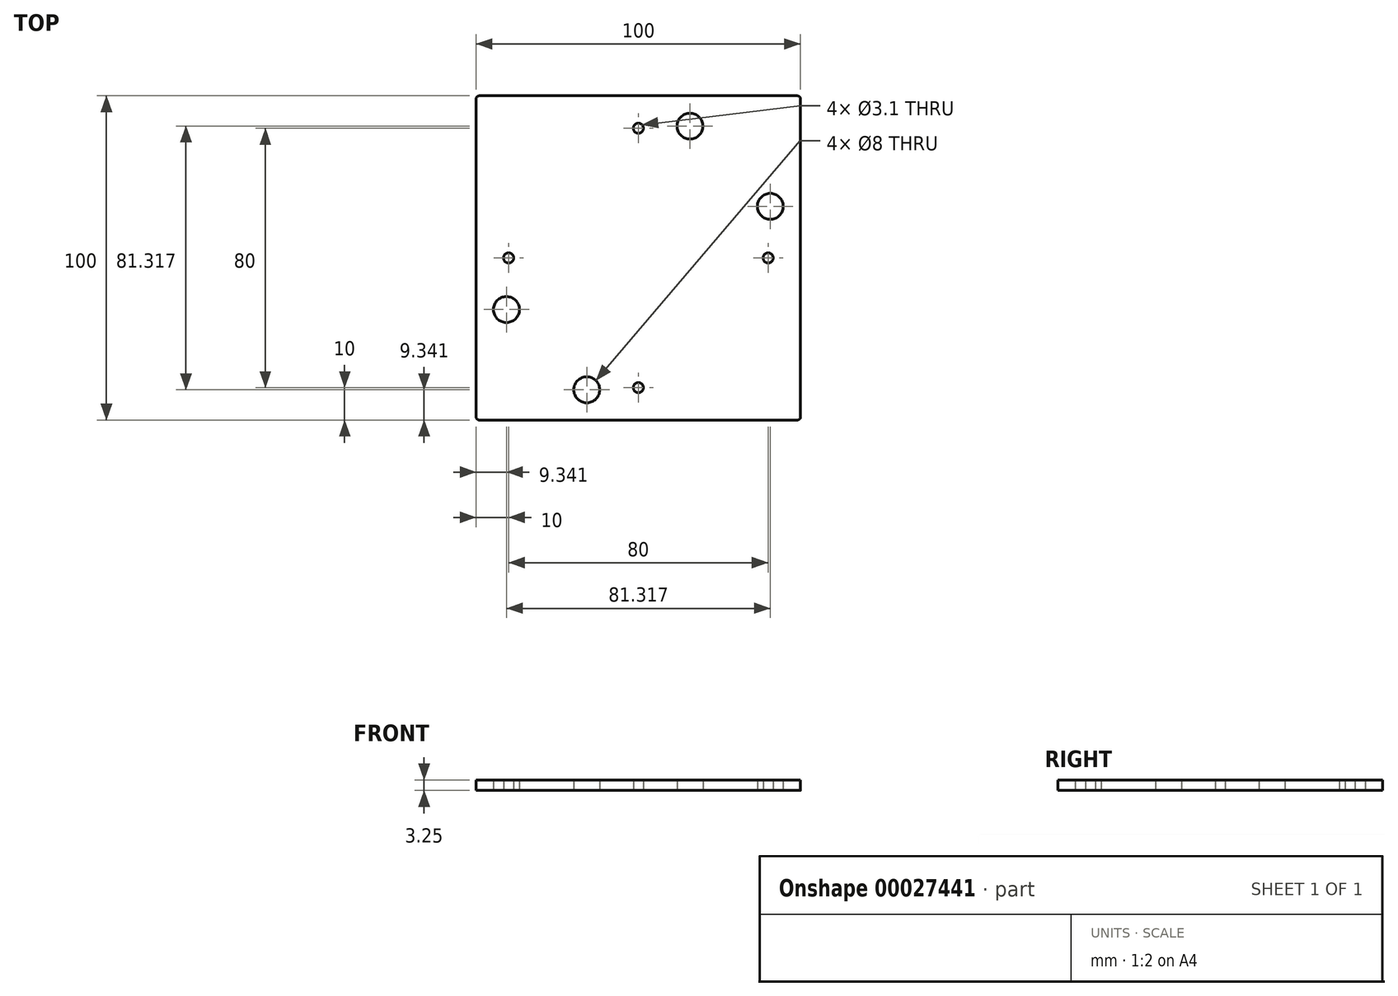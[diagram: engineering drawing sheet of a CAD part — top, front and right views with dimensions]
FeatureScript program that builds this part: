
annotation { "Feature Type Name" : "Feature", "Feature Type Description" : "" }
export const myFeature = defineFeature(function(context is Context, id is Id, definition is map)
    precondition{}
    {
        {
            var Q0;
            Q0=qCreatedBy(makeId("Top.planeOp"),FACE);
            var sketch = newSketch(context, id + "F0", { "sketchPlane" : qUnion([Q0])});
            skLineSegment(sketch, "E0.rect.bottom", {"start": v(-50, 50) * mm, "end": v(50, 50) * mm});
            skLineSegment(sketch, "E0.rect.top", {"start": v(-50, -50) * mm, "end": v(50, -50) * mm});
            skLineSegment(sketch, "E0.rect.left", {"start": v(-50, 50) * mm, "end": v(-50, -50) * mm});
            skLineSegment(sketch, "E0.rect.right", {"start": v(50, 50) * mm, "end": v(50, -50) * mm});
            skPoint(sketch, "E0.rect.middle", {"position": v(0, 0) * mm});
            skLineSegment(sketch, "E1", {"start": v(-50, 0) * mm, "end": v(50, 0) * mm, "construction": true});
            skLineSegment(sketch, "E2", {"start": v(0, 50) * mm, "end": v(0, -50) * mm, "construction": true});
            skPoint(sketch, "E2.endSnap0", {"position": v(0, -50) * mm});
            skCircle(sketch, "E3", {"center": v(-40, 0) * mm, "radius": 1.55 * mm});
            skCircle(sketch, "E4.1.0", {"center": v(0, -40) * mm, "radius": 1.55 * mm});
            skCircle(sketch, "E4.2.0", {"center": v(40, 0) * mm, "radius": 1.55 * mm});
            skCircle(sketch, "E4.3.0", {"center": v(0, 40) * mm, "radius": 1.55 * mm});
            skLineSegment(sketch, "E5", {"start": v(25.25, 50) * mm, "end": v(-50, -25.25) * mm, "construction": true});
            skLineSegment(sketch, "E6", {"start": v(-25.25, -50) * mm, "end": v(50, 25.25) * mm, "construction": true});
            skCircle(sketch, "E7", {"center": v(15.9, 40.66) * mm, "radius": 4 * mm});
            skLineSegment(sketch, "E8", {"start": v(15.9, 40.66) * mm, "end": v(40.66, 15.9) * mm, "construction": true});
            skLineSegment(sketch, "E9", {"start": v(-40.66, -15.9) * mm, "end": v(-15.9, -40.66) * mm, "construction": true});
            skCircle(sketch, "E10", {"center": v(-40.66, -15.9) * mm, "radius": 4 * mm});
            skCircle(sketch, "E11", {"center": v(-15.9, -40.66) * mm, "radius": 4 * mm});
            skCircle(sketch, "E12", {"center": v(40.66, 15.9) * mm, "radius": 4 * mm});
            skLineSegment(sketch, "E13", {"start": v(-15.9, -40.66) * mm, "end": v(-25.25, -50) * mm, "construction": true});
            skLineSegment(sketch, "E14", {"start": v(40.66, 15.9) * mm, "end": v(50, 25.25) * mm, "construction": true});
            skSolve(sketch);
        }
        {
            var Q0;
            Q0=qSketchRegion(id+"F0",true);
            extrude(context, id + "F1", {"entities" : qUnion([Q0]), "depth" : 3.25 * mm});
        }
        {
            var Q0;
            Q0=makeQuery(id+"F1.opExtrude","SWEPT_EDGE",EDGE,{"disambiguationData":[OSD([sQuery(id+"F0.wireOp",EDGE,"E0.rect.top"),sQuery(id+"F0.wireOp",EDGE,"E0.rect.left")])]});
            var Q1;
            Q1=makeQuery(id+"F1.opExtrude","SWEPT_EDGE",EDGE,{"disambiguationData":[OSD([sQuery(id+"F0.wireOp",EDGE,"E0.rect.top"),sQuery(id+"F0.wireOp",EDGE,"E0.rect.right")])]});
            var Q2;
            Q2=makeQuery(id+"F1.opExtrude","SWEPT_EDGE",EDGE,{"disambiguationData":[OSD([sQuery(id+"F0.wireOp",EDGE,"E0.rect.bottom"),sQuery(id+"F0.wireOp",EDGE,"E0.rect.right")])]});
            var Q3;
            Q3=makeQuery(id+"F1.opExtrude","SWEPT_EDGE",EDGE,{"disambiguationData":[OSD([sQuery(id+"F0.wireOp",EDGE,"E0.rect.bottom"),sQuery(id+"F0.wireOp",EDGE,"E0.rect.left")])]});
            fillet(context, id + "F2", {"entities" : qUnion([Q0, Q1, Q2, Q3]), "radius" : 1 * mm, "tangentPropagation" : true, "allowEdgeOverflow" : false});
        }
    });
